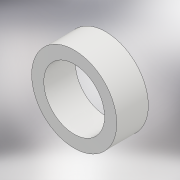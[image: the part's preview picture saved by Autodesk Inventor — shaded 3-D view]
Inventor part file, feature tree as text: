
AUTODESK INVENTOR PART (.ipt)
format: ipt  version: 2018.2 (Build 222227000, 227)  size: 108,544 bytes
history: native  units: mm
features: extrude x1, sketch x1
ambient origin geometry x8: Origin, YZ Plane, XZ Plane, XY Plane, X Axis, Y Axis, Z Axis, Center Point
bodies: Solid1 (feature_tree)
feature tree (2):
  extrude  "Extrusion1"  Depth=10.0mm
  sketch  "Sketch1"  dims[d0=5.2mm d1=0.0mm d2=10.0mm d3=14.0mm]
